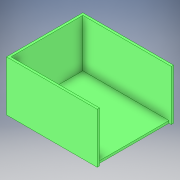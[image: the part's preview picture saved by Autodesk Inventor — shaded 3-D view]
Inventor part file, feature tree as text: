
AUTODESK INVENTOR PART (.ipt)
format: ipt  version: 2019 (Build 230136000, 136)  size: 125,440 bytes
history: native  units: mm
features: extrude x2, sketch x2, projected_geometry x1
ambient origin geometry x8: Origin, YZ Plane, XZ Plane, XY Plane, X Axis, Y Axis, Z Axis, Center Point
bodies: Solid1 (feature_tree)
feature tree (5):
  extrude  "Extrusion1"  Depth=100.0mm
  extrude  "Extrusion2"  Depth=3.18mm
  sketch  "Sketch1"  dims[d0=120.0mm d1=100.0mm]
  sketch  "Sketch2"  dims[d2=3.18mm d3=0.0mm d4=3.18mm d5=3.18mm d6=3.18mm d7=3.18mm d8=70.0mm d9=0.0mm]
  projected_geometry  "Projected Loop1"
